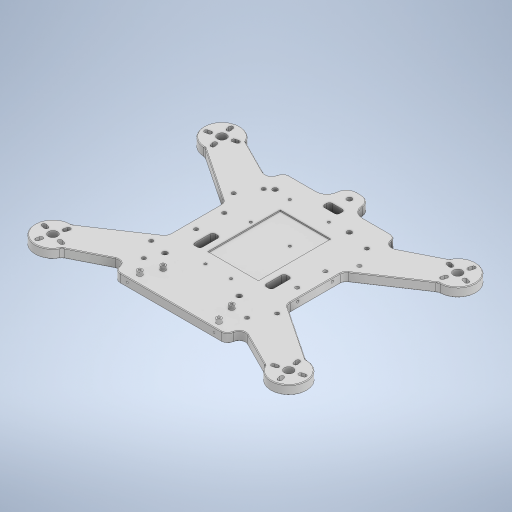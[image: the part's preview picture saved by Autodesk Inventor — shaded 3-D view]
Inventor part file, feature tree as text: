
AUTODESK INVENTOR PART (.ipt)
format: ipt  version: 2023.2 (Build 272271030, 271C)  size: 1,457,152 bytes
history: native  units: mm
features: extrude x14, projected_geometry x13, sketch x12, fillet x5, plane x3
ambient origin geometry x8: Origin, YZ Plane, XZ Plane, XY Plane, X Axis, Y Axis, Z Axis, Center Point
bodies: Body1 (feature_tree)
feature tree (47):
  sketch  "Sketch1"  dims[d28=39.5mm d29=39.5mm]
  extrude  "Extrusion-intel_d4"  Depth=39.5mm
  extrude  "Extrusion-airframe"  Depth=4.0mm
  fillet  "Fillet-gps"  Radius=3.75mm
  fillet  "Fillet-edges_airframe"  Radius=4.0mm
  fillet  "Fillet8"  Radius=3.75mm
  plane  "Work Plane2"
  sketch  "Sketch4"  dims[d30=100.0mm d36=4.0mm d37=3.75mm d38=4.0mm d39=3.75mm d40=58.0mm]
  extrude  "intel-realsense-holes"  Depth=86.0mm
  sketch  "Sketch10"  dims[d45=58.0mm d46=17.0mm]
  plane  "Work Plane3"
  extrude  "Extrusion15"  Depth=17.0mm
  extrude  "Extrusion16"  Depth=3.75mm
  sketch  "Sketch16"  dims[d77=0.0mm d79=84.5mm d81=28.0mm]
  fillet  "Fillet11"  Radius=50.0mm
  fillet  "Fillet12"  Radius=5.0mm
  plane  "Work Plane4"
  extrude  "Extrusion18"  Depth=28.0mm
  extrude  "Extrusion19"  Depth=44.0mm
  extrude  "Extrusion20"  Depth=15.0mm
  extrude  "Extrusion21"  Depth=89.0mm
  extrude  "Extrusion22"  Depth=66.0mm
  extrude  "Extrusion23"  Depth=10.0mm
  extrude  "Extrusion24"  Depth=10.0mm
  sketch  "Sketch21"  dims[d135=3.0mm d157=1.1mm d160=1.7mm d163=7.0mm d167=1.7mm d170=1.0mm d176=89.0mm]
  sketch  "Sketch23"  dims[d177=132.113536mm d178=66.0mm]
  extrude  "Extrusion27"  Depth=10.0mm
  extrude  "Extrusion28"  Depth=10.0mm
  sketch  "Sketch5"  dims[d41=3.75mm d42=86.0mm d44=86.0mm]
  sketch  "Sketch15"  dims[d47=4.0mm d48=3.75mm d54=50.0mm d67=5.0mm]
  projected_geometry  "Projected Loop1"
  projected_geometry  "Projected Loop2"
  projected_geometry  "Projected Loop3"
  projected_geometry  "Projected Loop4"
  projected_geometry  "Projected Loop5"
  projected_geometry  "Projected Loop6"
  sketch  "Sketch17"  dims[d84=55.0mm d102=44.0mm]
  projected_geometry  "Projected Loop7"
  sketch  "Sketch18"  dims[d108=20.0mm d109=15.0mm]
  sketch  "Sketch20"  dims[d110=0.0mm d111=10.0mm]
  projected_geometry  "Projected Loop8"
  projected_geometry  "Projected Loop9"
  sketch  "Sketch24"  dims[d179=184.262794mm d180=184.262794mm d181=132.0mm d182=7.5mm d183=4.0mm d186=3.0mm d187=45.0deg d188=30.9mm d189=3.0mm d190=3.0mm d191=3.0mm d192=3.0mm d193=20.0mm d195=90.0deg d198=6.0mm d199=6.0mm d200=12.0mm d201=2.0mm d206=10.0mm d207=0.0mm d208=7.0mm d209=0.0mm d214=8.0mm d215=5.0mm d216=0.5mm d218=2.2mm d230=40.0mm d232=20.0mm d233=72.0mm d234=2.2mm d235=16.0mm d237=4.0mm d240=4.0mm d242=4.0mm d243=60.4mm d244=1.7mm d245=6.0mm d246=5.0mm d248=1.7mm d249=66.1mm d258=22.804mm d259=50.0mm d260=60.0mm d261=80.0mm d262=40.0mm d263=30.0mm d264=2.0mm d265=2.0mm d266=12.0mm d267=4.2mm d271=1.5mm d272=5.6mm d273=3.0mm d274=1.5mm d275=67.8mm d276=3.0mm d277=5.0mm d278=0.0mm d299=19.5mm d313=2.5mm d314=2.5mm d315=4.0mm d316=3.5mm d317=15.0mm d335=4.0mm d336=2.0mm d337=2.0mm d338=2.0mm d339=2.0mm d340=2.0mm d341=2.0mm d342=2.0mm d343=2.0mm d344=2.0mm d345=6.0mm d346=0.0mm d347=2.0mm d348=2.0mm d349=2.0mm d350=2.0mm d351=4.0mm d352=0.0mm d354=0.220645mm d358=20.0mm d359=15.0mm d360=18.322466mm d361=3.0mm d362=40.0mm d364=360.0deg d366=3.0mm d367=40.0mm d369=360.0deg d371=7.0mm d372=40.0mm d374=360.0deg d377=22.0mm d378=5.0mm d379=4.0mm d381=35.8mm d382=2.0mm d383=2.0mm d386=6.0mm d387=10.0mm d389=20.0mm d390=10.0mm d391=0.0mm d392=56.5mm d393=39.5mm d394=6.0mm d395=0.0mm d396=7.0mm d397=0.0mm d398=6.0mm d400=2.0mm d401=7.0mm d402=0.0mm d405=2.0mm d406=2.0mm d407=2.0mm d408=2.0mm d409=30.5mm d410=30.5mm d413=30.5mm d414=30.5mm d415=23.0mm d416=41.0mm d417=76.0mm d418=8.0mm d419=1.0mm d420=2.0mm d421=38.0mm d422=20.5mm d423=2.0mm d424=2.0mm d426=20.0mm d427=10.5mm d428=0.0mm d429=0.0mm d430=0.0mm d431=0.0mm d432=13.0mm d433=3.0mm d434=3.0mm d435=0.0mm d436=0.0mm d455=2.0mm d456=4.0mm d457=27.0mm d458=39.011167mm d459=6.0mm d460=6.0mm d461=0.0mm d462=2.0mm d463=44.351371mm d464=3.0mm d465=7.0mm d466=3.0mm d467=22.0mm d468=0.0mm d469=0.0mm d68=0.872665mm d69=0.5mm d70=0.872665mm d96=0.5mm d97=0.872665mm d98=0.5mm d99=0.872665mm d100=0.0mm d101=0.0mm]
  projected_geometry  "Project Cut Edges1"
  projected_geometry  "Project Cut Edges2"
  projected_geometry  "Project Cut Edges3"
  projected_geometry  "Project Cut Edges4"
